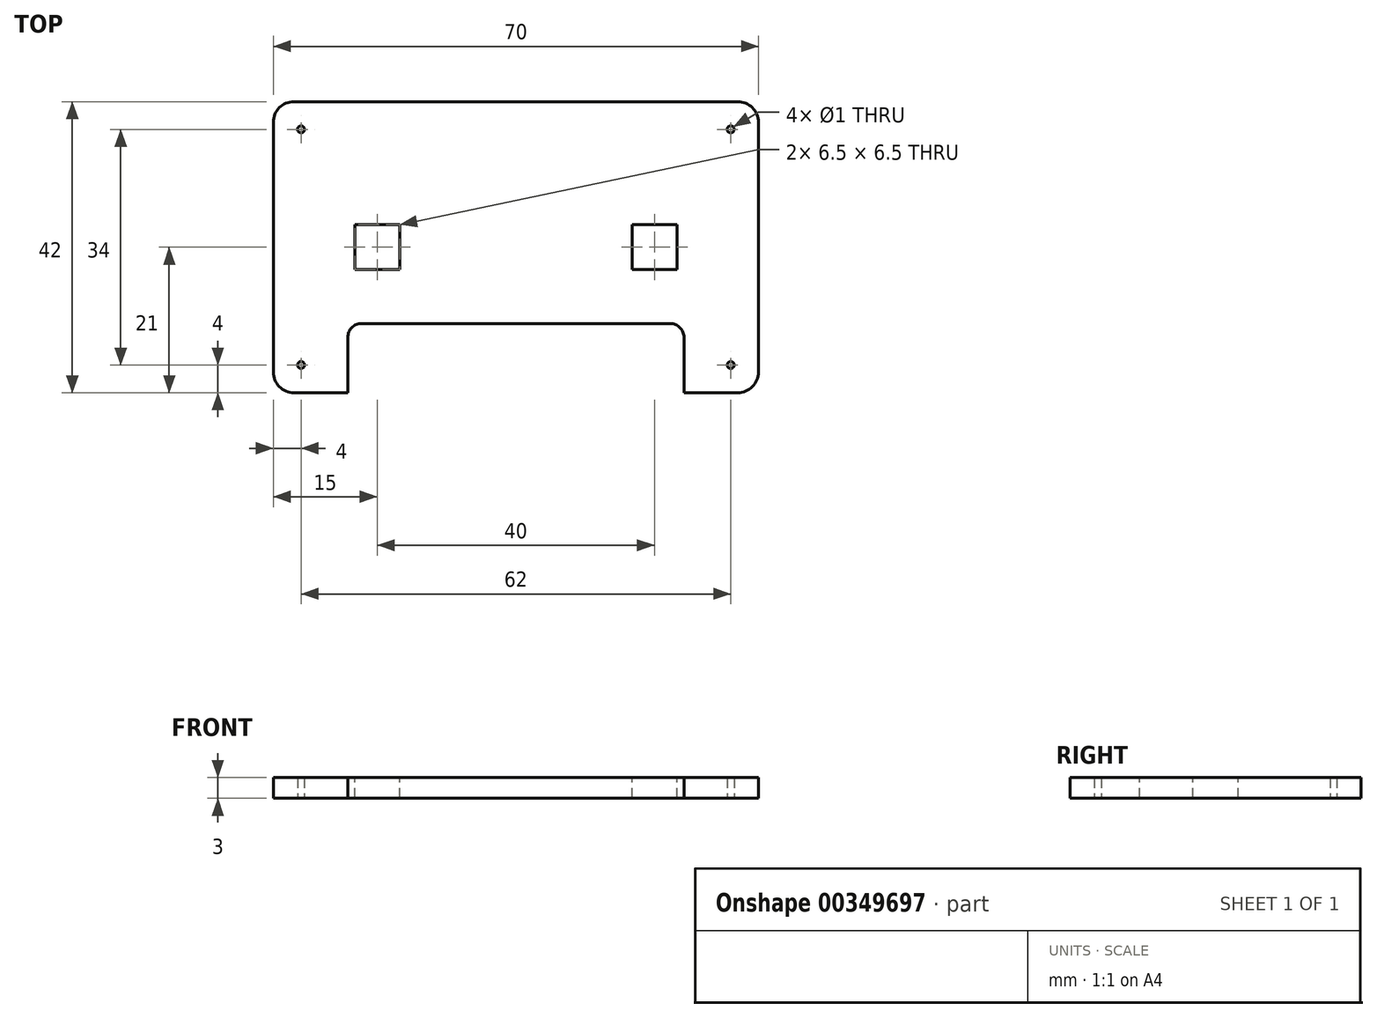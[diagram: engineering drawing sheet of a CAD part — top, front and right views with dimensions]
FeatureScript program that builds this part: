
annotation { "Feature Type Name" : "Feature", "Feature Type Description" : "" }
export const myFeature = defineFeature(function(context is Context, id is Id, definition is map)
    precondition{}
    {
        {
            var Q0;
            Q0=qCreatedBy(makeId("Top.planeOp"),FACE);
            var sketch = newSketch(context, id + "F0", { "sketchPlane" : qUnion([Q0])});
            skLineSegment(sketch, "E0.bottom", {"start": v(3, 0) * mm, "end": v(67, 0) * mm});
            skLineSegment(sketch, "E0.top", {"start": v(3, 42) * mm, "end": v(67, 42) * mm});
            skLineSegment(sketch, "E0.left", {"start": v(0, 3) * mm, "end": v(0, 39) * mm});
            skLineSegment(sketch, "E0.right", {"start": v(70, 3) * mm, "end": v(70, 39) * mm});
            skPoint(sketch, "E1.visualSharp", {"position": v(0, 42) * mm});
            skArc(sketch, "E1.filletArc", {"start": v(3, 42) * mm, "mid": v(0.88, 41.12) * mm, "end": v(0, 39) * mm});
            skPoint(sketch, "E2.visualSharp", {"position": v(70, 42) * mm});
            skArc(sketch, "E2.filletArc", {"start": v(70, 39) * mm, "mid": v(69.12, 41.12) * mm, "end": v(67, 42) * mm});
            skPoint(sketch, "E3.visualSharp", {"position": v(0, 0) * mm});
            skArc(sketch, "E3.filletArc", {"start": v(0, 3) * mm, "mid": v(0.88, 0.88) * mm, "end": v(3, 0) * mm});
            skPoint(sketch, "E4.visualSharp", {"position": v(70, 0) * mm});
            skArc(sketch, "E4.filletArc", {"start": v(67, 0) * mm, "mid": v(69.12, 0.88) * mm, "end": v(70, 3) * mm});
            skSolve(sketch);
        }
        {
            var Q0;
            Q0=makeQuery(id+"F0.imprint","IMPRINT",FACE,{"disambiguationData":[TD([[makeQuery(id+"F0.imprint","IMPRINT",EDGE,{"derivedFrom":sQuery(id+"F0.wireOp",EDGE,"E0.bottom")}),1.0]])]});
            extrude(context, id + "F1", {"entities" : qUnion([Q0]), "depth" : 3 * mm});
        }
        {
            var Q0;
            Q0=makeQuery(id+"F1.opExtrude","CAP_FACE",FACE,{"disambiguationData":[OSD([sQuery(id+"F0.wireOp",EDGE,"E0.bottom"),sQuery(id+"F0.wireOp",EDGE,"E0.top"),sQuery(id+"F0.wireOp",EDGE,"E0.left"),sQuery(id+"F0.wireOp",EDGE,"E0.right"),sQuery(id+"F0.wireOp",EDGE,"E1.filletArc"),sQuery(id+"F0.wireOp",EDGE,"E2.filletArc"),sQuery(id+"F0.wireOp",EDGE,"E3.filletArc"),sQuery(id+"F0.wireOp",EDGE,"E4.filletArc")])],"isStart":false});
            var sketch = newSketch(context, id + "F2", { "sketchPlane" : qUnion([Q0])});
            skPoint(sketch, "E5", {"position": v(35, 7) * mm});
            skPoint(sketch, "E5.positionSnap0", {"position": v(35, 0) * mm});
            skPoint(sketch, "E6", {"position": v(45.5, 7) * mm});
            skPoint(sketch, "E7", {"position": v(56, 7) * mm});
            skPoint(sketch, "E8", {"position": v(24.5, 7) * mm});
            skPoint(sketch, "E9", {"position": v(14, 7) * mm});
            skSolve(sketch);
        }
        {
            var Q0;
            Q0=sQuery(id+"F2.wireOp",VERTEX,"E9");
            var Q1;
            Q1=sQuery(id+"F2.wireOp",VERTEX,"E8");
            var Q2;
            Q2=sQuery(id+"F2.wireOp",VERTEX,"E5");
            var Q3;
            Q3=sQuery(id+"F2.wireOp",VERTEX,"E6");
            var Q4;
            Q4=sQuery(id+"F2.wireOp",VERTEX,"E7");
            var Q5;
            Q5=makeQuery(id+"F1.opExtrude","SWEPT_BODY",BODY,{"disambiguationData":[OSD([sQuery(id+"F0.wireOp",EDGE,"E0.bottom"),sQuery(id+"F0.wireOp",EDGE,"E0.top"),sQuery(id+"F0.wireOp",EDGE,"E0.left"),sQuery(id+"F0.wireOp",EDGE,"E0.right"),sQuery(id+"F0.wireOp",EDGE,"E1.filletArc"),sQuery(id+"F0.wireOp",EDGE,"E2.filletArc"),sQuery(id+"F0.wireOp",EDGE,"E3.filletArc"),sQuery(id+"F0.wireOp",EDGE,"E4.filletArc")])]});
            hole(context, id + "F3", {"style" : HoleStyle.SIMPLE, "endStyle" : HoleEndStyle.THROUGH, "holeDiameter" : 4 * mm, "isTappedThrough" : true, "tappedDepth" : 12 * mm, "tapClearance" : 3, "locations" : qUnion([Q0, Q1, Q2, Q3, Q4]), "scope" : qUnion([Q5])});
        }
        {
            var Q0;
            Q0=makeQuery(id+"F1.opExtrude","CAP_FACE",FACE,{"disambiguationData":[OSD([sQuery(id+"F0.wireOp",EDGE,"E0.bottom"),sQuery(id+"F0.wireOp",EDGE,"E0.top"),sQuery(id+"F0.wireOp",EDGE,"E0.left"),sQuery(id+"F0.wireOp",EDGE,"E0.right"),sQuery(id+"F0.wireOp",EDGE,"E1.filletArc"),sQuery(id+"F0.wireOp",EDGE,"E2.filletArc"),sQuery(id+"F0.wireOp",EDGE,"E3.filletArc"),sQuery(id+"F0.wireOp",EDGE,"E4.filletArc")])],"isStart":false});
            var sketch = newSketch(context, id + "F4", { "sketchPlane" : qUnion([Q0])});
            skLineSegment(sketch, "E10.bottom", {"start": v(11.75, 24.25) * mm, "end": v(18.25, 24.25) * mm});
            skLineSegment(sketch, "E10.top", {"start": v(11.75, 17.75) * mm, "end": v(18.25, 17.75) * mm});
            skLineSegment(sketch, "E10.left", {"start": v(11.75, 24.25) * mm, "end": v(11.75, 17.75) * mm});
            skLineSegment(sketch, "E10.right", {"start": v(18.25, 24.25) * mm, "end": v(18.25, 17.75) * mm});
            skPoint(sketch, "E10.middle", {"position": v(15, 21) * mm});
            skLineSegment(sketch, "E11", {"start": v(35, 47.91) * mm, "end": v(35, -7) * mm, "construction": true});
            skPoint(sketch, "E11.startSnap0", {"position": v(35, 42) * mm});
            skLineSegment(sketch, "E12.MirrorCS", {"start": v(58.25, 24.25) * mm, "end": v(51.75, 24.25) * mm});
            skLineSegment(sketch, "E13.MirrorCS", {"start": v(51.75, 24.25) * mm, "end": v(51.75, 17.75) * mm});
            skLineSegment(sketch, "E14.MirrorCS", {"start": v(58.25, 17.75) * mm, "end": v(51.75, 17.75) * mm});
            skLineSegment(sketch, "E15.MirrorCS", {"start": v(58.25, 24.25) * mm, "end": v(58.25, 17.75) * mm});
            skPoint(sketch, "E16.MirrorP", {"position": v(55, 21) * mm});
            skSolve(sketch);
        }
        {
            var Q0;
            Q0=makeQuery(id+"F4.imprint","IMPRINT",FACE,{"disambiguationData":[TD([[makeQuery(id+"F4.imprint","IMPRINT",EDGE,{"derivedFrom":sQuery(id+"F4.wireOp",EDGE,"E10.bottom")}),-1.0]])]});
            var Q1;
            Q1=makeQuery(id+"F4.imprint","IMPRINT",FACE,{"disambiguationData":[TD([[makeQuery(id+"F4.imprint","IMPRINT",EDGE,{"derivedFrom":sQuery(id+"F4.wireOp",EDGE,"E12.MirrorCS")}),1.0]])]});
            extrude(context, id + "F5", {"entities" : qUnion([Q0, Q1]), "operationType" : NewBodyOperationType.REMOVE, "endBound" : BoundingType.UP_TO_NEXT, "oppositeDirection" : true, "depth" : 25 * mm});
        }
        {
            var Q0;
            Q0=makeQuery(id+"F1.opExtrude","CAP_FACE",FACE,{"disambiguationData":[OSD([sQuery(id+"F0.wireOp",EDGE,"E0.bottom"),sQuery(id+"F0.wireOp",EDGE,"E0.top"),sQuery(id+"F0.wireOp",EDGE,"E0.left"),sQuery(id+"F0.wireOp",EDGE,"E0.right"),sQuery(id+"F0.wireOp",EDGE,"E1.filletArc"),sQuery(id+"F0.wireOp",EDGE,"E2.filletArc"),sQuery(id+"F0.wireOp",EDGE,"E3.filletArc"),sQuery(id+"F0.wireOp",EDGE,"E4.filletArc")])],"isStart":false});
            var sketch = newSketch(context, id + "F6", { "sketchPlane" : qUnion([Q0])});
            skLineSegment(sketch, "E17.bottom", {"start": v(12.75, 10) * mm, "end": v(57.25, 10) * mm});
            skLineSegment(sketch, "E17.top", {"start": v(10.75, -10) * mm, "end": v(59.25, -10) * mm});
            skLineSegment(sketch, "E17.left", {"start": v(10.75, 8) * mm, "end": v(10.75, -10) * mm});
            skLineSegment(sketch, "E17.right", {"start": v(59.25, 8) * mm, "end": v(59.25, -10) * mm});
            skPoint(sketch, "E17.middle", {"position": v(35, 0) * mm});
            skPoint(sketch, "E18.visualSharp", {"position": v(10.75, 10) * mm});
            skArc(sketch, "E18.filletArc", {"start": v(12.75, 10) * mm, "mid": v(11.34, 9.41) * mm, "end": v(10.75, 8) * mm});
            skPoint(sketch, "E19.visualSharp", {"position": v(59.25, 10) * mm});
            skArc(sketch, "E19.filletArc", {"start": v(59.25, 8) * mm, "mid": v(58.66, 9.41) * mm, "end": v(57.25, 10) * mm});
            skSolve(sketch);
        }
        {
            var Q0;
            Q0=makeQuery(id+"F6.imprint","IMPRINT",FACE,{"disambiguationData":[TD([[makeQuery(id+"F6.imprint","IMPRINT",EDGE,{"derivedFrom":sQuery(id+"F6.wireOp",EDGE,"E17.bottom")}),-1.0]])]});
            extrude(context, id + "F7", {"entities" : qUnion([Q0]), "operationType" : NewBodyOperationType.REMOVE, "endBound" : BoundingType.THROUGH_ALL, "oppositeDirection" : true, "depth" : 25 * mm});
        }
        {
            var Q0;
            Q0=makeQuery(id+"F1.opExtrude","CAP_FACE",FACE,{"disambiguationData":[OSD([sQuery(id+"F0.wireOp",EDGE,"E0.bottom"),sQuery(id+"F0.wireOp",EDGE,"E0.top"),sQuery(id+"F0.wireOp",EDGE,"E0.left"),sQuery(id+"F0.wireOp",EDGE,"E0.right"),sQuery(id+"F0.wireOp",EDGE,"E1.filletArc"),sQuery(id+"F0.wireOp",EDGE,"E2.filletArc"),sQuery(id+"F0.wireOp",EDGE,"E3.filletArc"),sQuery(id+"F0.wireOp",EDGE,"E4.filletArc")])],"isStart":false});
            var sketch = newSketch(context, id + "F8", { "sketchPlane" : qUnion([Q0])});
            skPoint(sketch, "E20", {"position": v(4, 4) * mm});
            skPoint(sketch, "E21", {"position": v(4, 38) * mm});
            skPoint(sketch, "E22", {"position": v(66, 38) * mm});
            skPoint(sketch, "E23", {"position": v(66, 4) * mm});
            skSolve(sketch);
        }
        {
            var Q0;
            Q0=sQuery(id+"F8.wireOp",VERTEX,"E21");
            var Q1;
            Q1=sQuery(id+"F8.wireOp",VERTEX,"E20");
            var Q2;
            Q2=sQuery(id+"F8.wireOp",VERTEX,"E23");
            var Q3;
            Q3=sQuery(id+"F8.wireOp",VERTEX,"E22");
            var Q4;
            Q4=makeQuery(id+"F1.opExtrude","SWEPT_BODY",BODY,{"disambiguationData":[OSD([sQuery(id+"F0.wireOp",EDGE,"E0.bottom"),sQuery(id+"F0.wireOp",EDGE,"E0.top"),sQuery(id+"F0.wireOp",EDGE,"E0.left"),sQuery(id+"F0.wireOp",EDGE,"E0.right"),sQuery(id+"F0.wireOp",EDGE,"E1.filletArc"),sQuery(id+"F0.wireOp",EDGE,"E2.filletArc"),sQuery(id+"F0.wireOp",EDGE,"E3.filletArc"),sQuery(id+"F0.wireOp",EDGE,"E4.filletArc")])]});
            hole(context, id + "F9", {"style" : HoleStyle.SIMPLE, "endStyle" : HoleEndStyle.THROUGH, "holeDiameter" : 1 * mm, "isTappedThrough" : true, "tappedDepth" : 12 * mm, "tapClearance" : 3, "locations" : qUnion([Q0, Q1, Q2, Q3]), "scope" : qUnion([Q4])});
        }
    });
